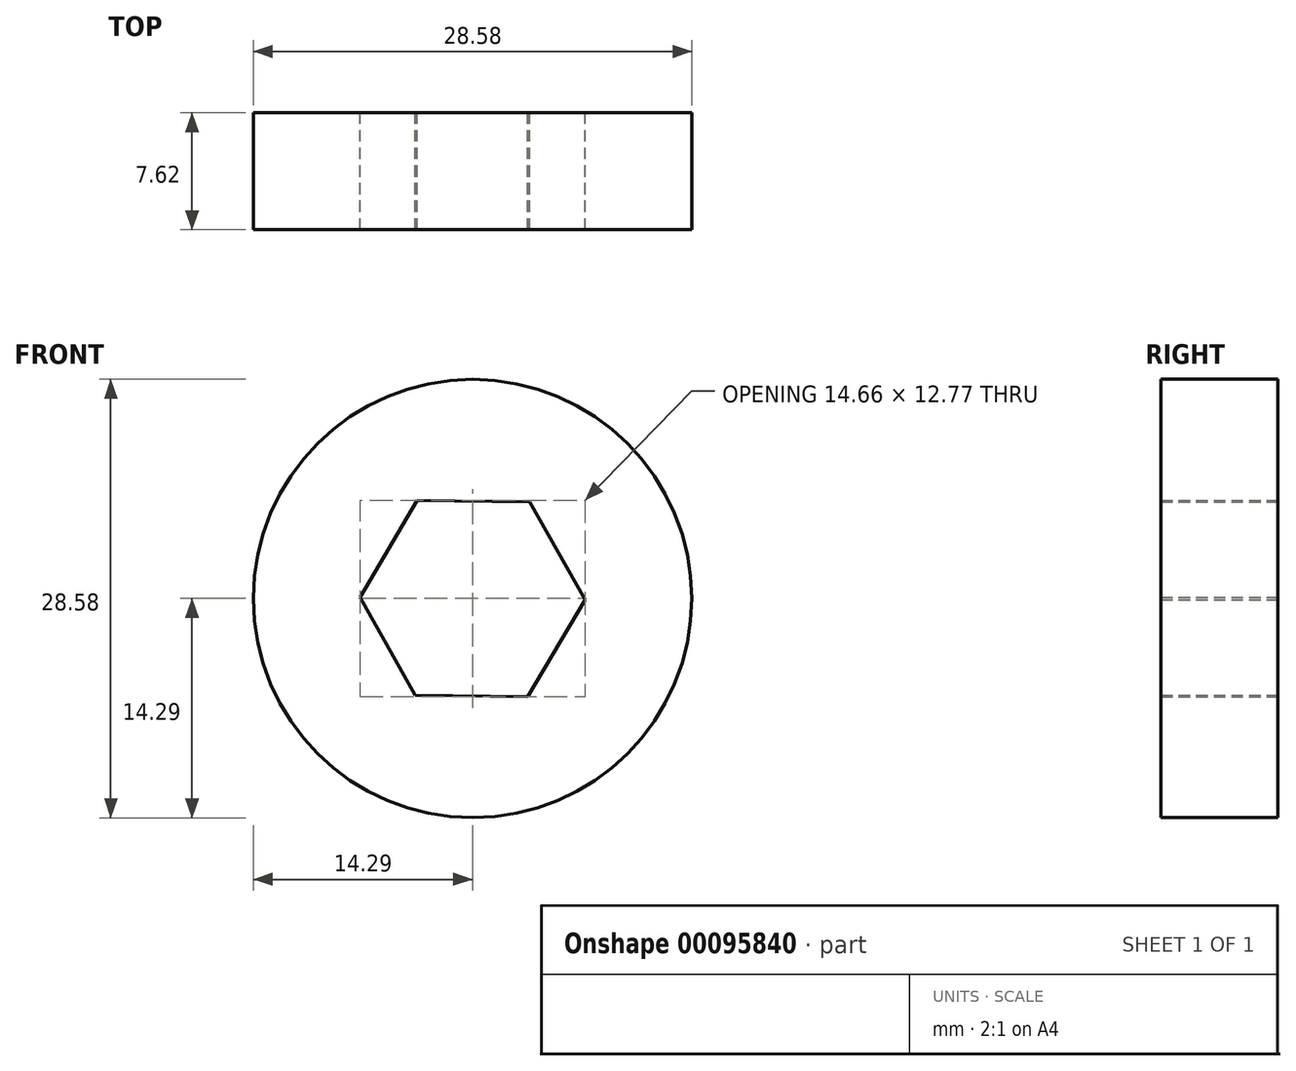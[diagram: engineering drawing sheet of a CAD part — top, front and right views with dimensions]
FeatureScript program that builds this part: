
annotation { "Feature Type Name" : "Feature", "Feature Type Description" : "" }
export const myFeature = defineFeature(function(context is Context, id is Id, definition is map)
    precondition{}
    {
        {
            var Q0;
            Q0=qCreatedBy(makeId("Front.planeOp"),FACE);
            var sketch = newSketch(context, id + "F0", { "sketchPlane" : qUnion([Q0])});
            skCircle(sketch, "E0", {"center": v(0, 0) * mm, "radius": 14.29 * mm});
            skCircle(sketch, "E1.cCircle", {"center": v(0, 0) * mm, "radius": 6.35 * mm, "construction": true});
            skLineSegment(sketch, "E1.0", {"start": v(3.73, 6.31) * mm, "end": v(7.33, -0.08) * mm});
            skLineSegment(sketch, "E1.1", {"start": v(7.33, -0.08) * mm, "end": v(3.6, -6.39) * mm});
            skLineSegment(sketch, "E1.2", {"start": v(3.6, -6.39) * mm, "end": v(-3.73, -6.31) * mm});
            skLineSegment(sketch, "E1.3", {"start": v(-3.73, -6.31) * mm, "end": v(-7.33, 0.08) * mm});
            skLineSegment(sketch, "E1.4", {"start": v(-7.33, 0.08) * mm, "end": v(-3.6, 6.39) * mm});
            skLineSegment(sketch, "E1.5", {"start": v(-3.6, 6.39) * mm, "end": v(3.73, 6.31) * mm});
            skPoint(sketch, "E1.0.midPoint", {"position": v(5.53, 3.12) * mm});
            skSolve(sketch);
        }
        {
            var Q0;
            Q0=qSketchRegion(id+"F0",true);
            extrude(context, id + "F1", {"entities" : qUnion([Q0]), "depth" : 7.62 * mm});
        }
    });
